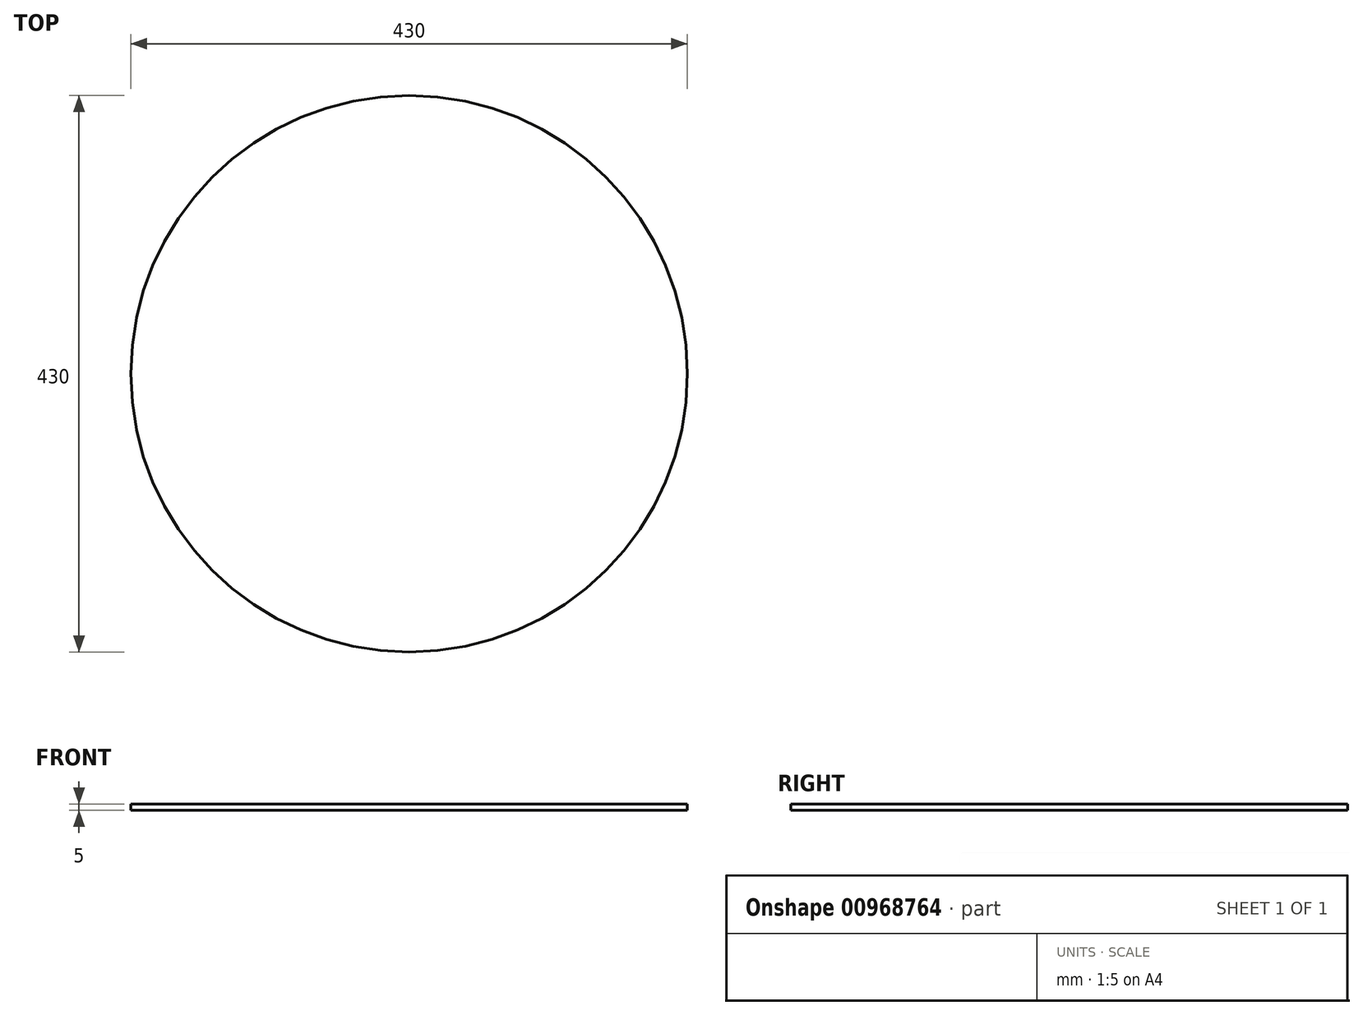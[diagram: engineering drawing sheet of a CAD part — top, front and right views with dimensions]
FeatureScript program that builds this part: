
annotation { "Feature Type Name" : "Feature", "Feature Type Description" : "" }
export const myFeature = defineFeature(function(context is Context, id is Id, definition is map)
    precondition{}
    {
        {
            var Q0;
            Q0=qCreatedBy(makeId("Top.planeOp"),FACE);
            var sketch = newSketch(context, id + "F0", { "sketchPlane" : qUnion([Q0])});
            skCircle(sketch, "E0", {"center": v(0, 0) * mm, "radius": 215 * mm});
            skSolve(sketch);
        }
        {
            var Q0;
            Q0 = qSketchRegion(id + "F0", true);
            extrude(context, id + "F1", {"entities" : qUnion([Q0]), "depth" : 5 * mm, "offsetDistance" : 25 * mm});
        }
    });
